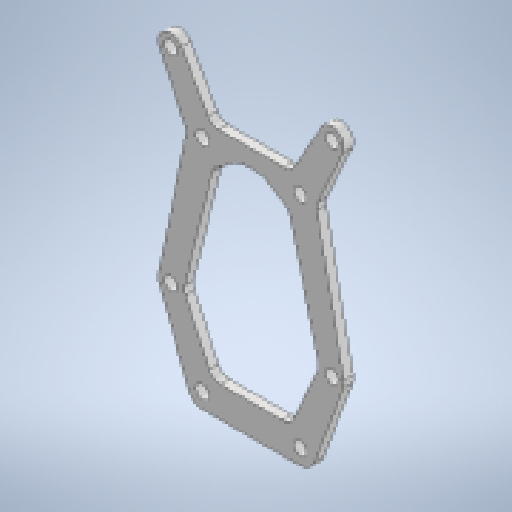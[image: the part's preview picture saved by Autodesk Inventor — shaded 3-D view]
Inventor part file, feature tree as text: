
AUTODESK INVENTOR PART (.ipt)
format: ipt  version: 2025.1 (Build 291241000, 241)  size: 230,912 bytes
history: native  units: mm
features: other x9, reference x9, extrude x1, fillet x1, sketch x1
ambient origin geometry x8: Origin, YZ Plane, XZ Plane, XY Plane, X Axis, Y Axis, Z Axis, Center Point
bodies: Body1 (feature_tree)
feature tree (21):
  other  "ソリッド1"
  extrude  "押し出し1"  Depth=2.2mm
  fillet  "フィレット1"  Radius=2.2mm
  sketch  "スケッチ1"
  reference  "参照1"
  reference  "参照2"
  reference  "参照3"
  reference  "参照4"
  reference  "参照5"
  reference  "参照6"
  reference  "参照7"
  reference  "参照8"
  reference  "参照9"
  other  "<userpath>\Documents\Inventor\Vixen\doutai.iam"
  other  "doutai.iam"
  other  "KRS2500_scale:1"
  other  "KSHI:1"
  other  "mata3:3"
  other  "mata3:4"
  other  "mata3:1"
  other  "mata3:2"
